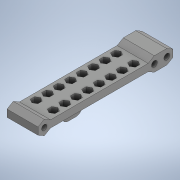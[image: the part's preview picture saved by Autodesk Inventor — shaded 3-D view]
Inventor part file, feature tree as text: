
AUTODESK INVENTOR PART (.ipt)
format: ipt  version: 2020 (Build 240168000, 168)  size: 486,912 bytes
history: native  units: in
note: dims shown in document units (in); Inventor stores cm internally (conversion verified against a paired STEP export)
features: sketch x7, extrude x6, projected_geometry x4, plane x2, mirror x1, fillet x1
ambient origin geometry x8: Origin, YZ Plane, XZ Plane, XY Plane, X Axis, Y Axis, Z Axis, Center Point
bodies: Solid1 (feature_tree)
feature tree (21):
  extrude  "Extrusion1"  Depth=3.4256in
  plane  "Work Plane1"
  extrude  "Extrusion2"  Depth=0.7874in
  sketch  "Sketch4"  dims[d4=0.0in d5=0.0827in]
  extrude  "Extrusion4"  Depth=0.0827in
  plane  "Work Plane2"
  extrude  "Extrusion6"  Depth=3.1106in
  mirror  "Mirror2"
  extrude  "Extrusion7"  Depth=0.315in
  extrude  "Extrusion8"  Depth=0.2362in
  fillet  "Fillet1"  [1 undecoded]
  sketch  "Sketch1"  dims[d0=0.1818in d1=3.4256in]
  sketch  "Sketch2"  dims[d2=0.1378in d3=0.7874in]
  sketch  "Sketch5"  dims[d6=0.7874in d7=0.0in d28=3.1106in]
  sketch  "Sketch7"  dims[d29=0.315in d31=0.315in]
  projected_geometry  "Projected Loop7"
  projected_geometry  "Projected Loop8"
  sketch  "Sketch8"  dims[d33=0.1476in d34=0.2362in d35=0.0in]
  projected_geometry  "Projected Loop9"
  sketch  "Sketch10"  dims[d38=0.315in d39=0.2756in d40=-0.3092in d41=0.0787in d42=0.0787in d43=0.0787in d44=3.1496in d46=0.2913in d47=0.3937in d49=0.3937in d51=3.1496in d53=0.2913in d54=0.3937in d56=0.3937in d58=0.0in d59=0.0in d60=1.0994in d61=0.1378in d63=1.1811in d64=0.1575in d65=0.0in d66=0.126in d67=0.1575in]
  projected_geometry  "Projected Loop10"
note: 1 required parameter value undecoded (feature->parameter linkage not recoverable at this tier; creation-order binding heuristic only, values carry confidence <= 0.55)
